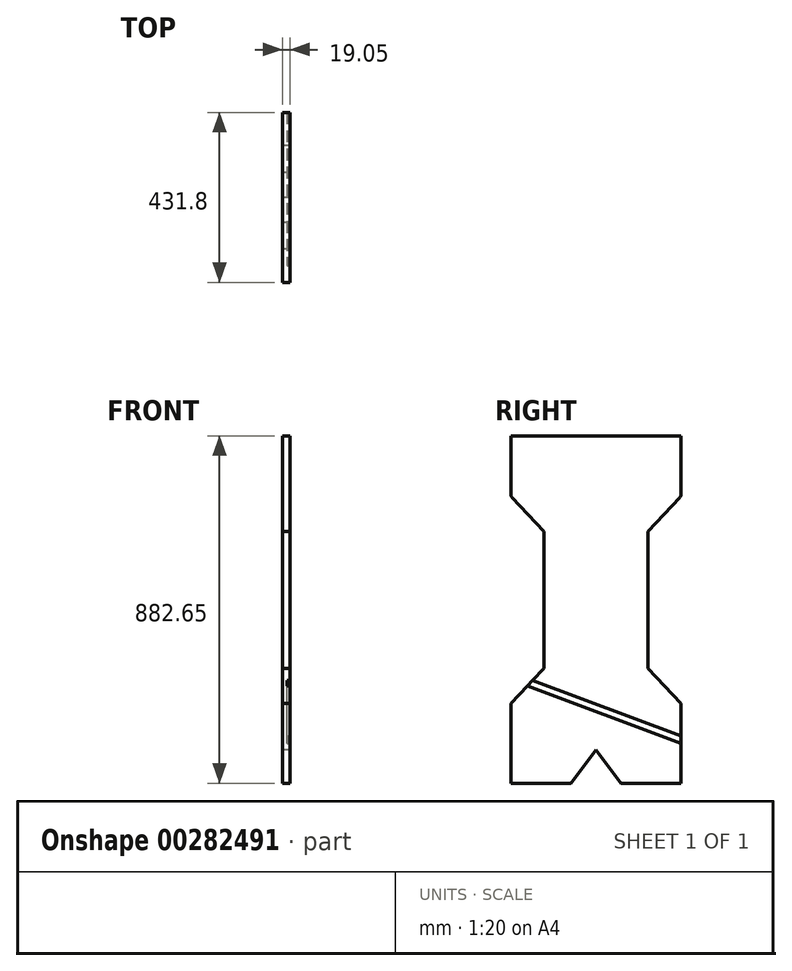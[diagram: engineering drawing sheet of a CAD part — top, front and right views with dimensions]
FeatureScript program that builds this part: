
annotation { "Feature Type Name" : "Feature", "Feature Type Description" : "" }
export const myFeature = defineFeature(function(context is Context, id is Id, definition is map)
    precondition{}
    {
        {
            var Q0;
            Q0=qCreatedBy(makeId("Right.planeOp"),FACE);
            var sketch = newSketch(context, id + "F0", { "sketchPlane" : qUnion([Q0])});
            skLineSegment(sketch, "E0.bottom", {"start": v(215.9, 76.83) * mm, "end": v(-215.9, 76.83) * mm});
            skLineSegment(sketch, "E0.top", {"start": v(215.9, -76.83) * mm, "end": v(-215.9, -76.83) * mm, "construction": true});
            skLineSegment(sketch, "E0.left", {"start": v(215.9, 76.83) * mm, "end": v(215.9, -72.8) * mm});
            skLineSegment(sketch, "E0.right", {"start": v(-215.9, 76.83) * mm, "end": v(-215.9, -73.26) * mm});
            skPoint(sketch, "E0.middle", {"position": v(0, 0) * mm});
            skLineSegment(sketch, "E1", {"start": v(-213.44, -79.43) * mm, "end": v(-131.55, -165.74) * mm});
            skLineSegment(sketch, "E2", {"start": v(213.12, -79.76) * mm, "end": v(131.55, -165.74) * mm});
            skLineSegment(sketch, "E3", {"start": v(-131.55, -165.74) * mm, "end": v(-131.55, -513.71) * mm});
            skPoint(sketch, "E4.visualSharp", {"position": v(-215.9, -76.83) * mm});
            skArc(sketch, "E4.filletArc", {"start": v(-215.9, -73.26) * mm, "mid": v(-215.26, -76.58) * mm, "end": v(-213.44, -79.43) * mm});
            skPoint(sketch, "E5.visualSharp", {"position": v(215.9, -76.83) * mm});
            skArc(sketch, "E5.filletArc", {"start": v(213.12, -79.76) * mm, "mid": v(215.18, -76.55) * mm, "end": v(215.9, -72.8) * mm});
            skLineSegment(sketch, "E6", {"start": v(-131.55, -513.71) * mm, "end": v(-215.9, -602.62) * mm});
            skLineSegment(sketch, "E7", {"start": v(-215.9, -602.62) * mm, "end": v(-215.9, -805.82) * mm});
            skLineSegment(sketch, "E8.MirrorCS", {"start": v(131.55, -165.74) * mm, "end": v(131.55, -513.71) * mm});
            skLineSegment(sketch, "E9.MirrorCS", {"start": v(131.55, -513.72) * mm, "end": v(215.9, -602.62) * mm});
            skLineSegment(sketch, "E10.MirrorCS", {"start": v(215.9, -602.62) * mm, "end": v(215.9, -805.82) * mm});
            skLineSegment(sketch, "E11", {"start": v(-131.55, -165.74) * mm, "end": v(-34.7, -165.74) * mm, "construction": true});
            skLineSegment(sketch, "E12", {"start": v(-215.9, -602.62) * mm, "end": v(-131.55, -602.62) * mm, "construction": true});
            skLineSegment(sketch, "E13", {"start": v(-215.9, -805.82) * mm, "end": v(-63.5, -805.82) * mm});
            skLineSegment(sketch, "E14", {"start": v(-63.5, -805.82) * mm, "end": v(0, -721.49) * mm});
            skLineSegment(sketch, "E15", {"start": v(0, -721.49) * mm, "end": v(63.5, -805.82) * mm});
            skLineSegment(sketch, "E16", {"start": v(63.5, -805.82) * mm, "end": v(215.9, -805.82) * mm});
            skSolve(sketch);
        }
        {
            var Q0;
            Q0=qSketchRegion(id+"F0",true);
            extrude(context, id + "F1", {"entities" : qUnion([Q0]), "depth" : 19.05 * mm});
        }
        {
            var Q0;
            Q0=makeQuery(id+"F1.opExtrude","CAP_FACE",FACE,{"disambiguationData":[OSD([sQuery(id+"F0.wireOp",EDGE,"E0.bottom"),sQuery(id+"F0.wireOp",EDGE,"E0.left"),sQuery(id+"F0.wireOp",EDGE,"E0.right"),sQuery(id+"F0.wireOp",EDGE,"E1"),sQuery(id+"F0.wireOp",EDGE,"E2"),sQuery(id+"F0.wireOp",EDGE,"E3"),sQuery(id+"F0.wireOp",EDGE,"E4.filletArc"),sQuery(id+"F0.wireOp",EDGE,"E5.filletArc"),sQuery(id+"F0.wireOp",EDGE,"E6"),sQuery(id+"F0.wireOp",EDGE,"E7"),sQuery(id+"F0.wireOp",EDGE,"E8.MirrorCS"),sQuery(id+"F0.wireOp",EDGE,"E9.MirrorCS"),sQuery(id+"F0.wireOp",EDGE,"E10.MirrorCS"),sQuery(id+"F0.wireOp",EDGE,"E13"),sQuery(id+"F0.wireOp",EDGE,"E14"),sQuery(id+"F0.wireOp",EDGE,"E15"),sQuery(id+"F0.wireOp",EDGE,"E16")])],"isStart":false});
            var sketch = newSketch(context, id + "F2", { "sketchPlane" : qUnion([Q0])});
            skLineSegment(sketch, "E17", {"start": v(215.9, -704.22) * mm, "end": v(-173.72, -558.17) * mm});
            skLineSegment(sketch, "E18", {"start": v(215.9, -685.17) * mm, "end": v(-160.61, -544.35) * mm});
            skLineSegment(sketch, "E19", {"start": v(-160.61, -544.35) * mm, "end": v(-173.72, -558.17) * mm});
            skSolve(sketch);
        }
        {
            var Q0;
            {var subQ0=sQuery(id+"F2.wireOp",EDGE,"E17");Q0=makeQuery(id+"F2.imprint","IMPRINT",FACE,{"disambiguationData":[TD([[makeQuery(id+"F2.imprint","IMPRINT",EDGE,{"derivedFrom":subQ0}),-1.0]])]});}
            extrude(context, id + "F3", {"entities" : qUnion([Q0]), "operationType" : NewBodyOperationType.REMOVE, "oppositeDirection" : true, "depth" : 7.62 * mm});
        }
    });
